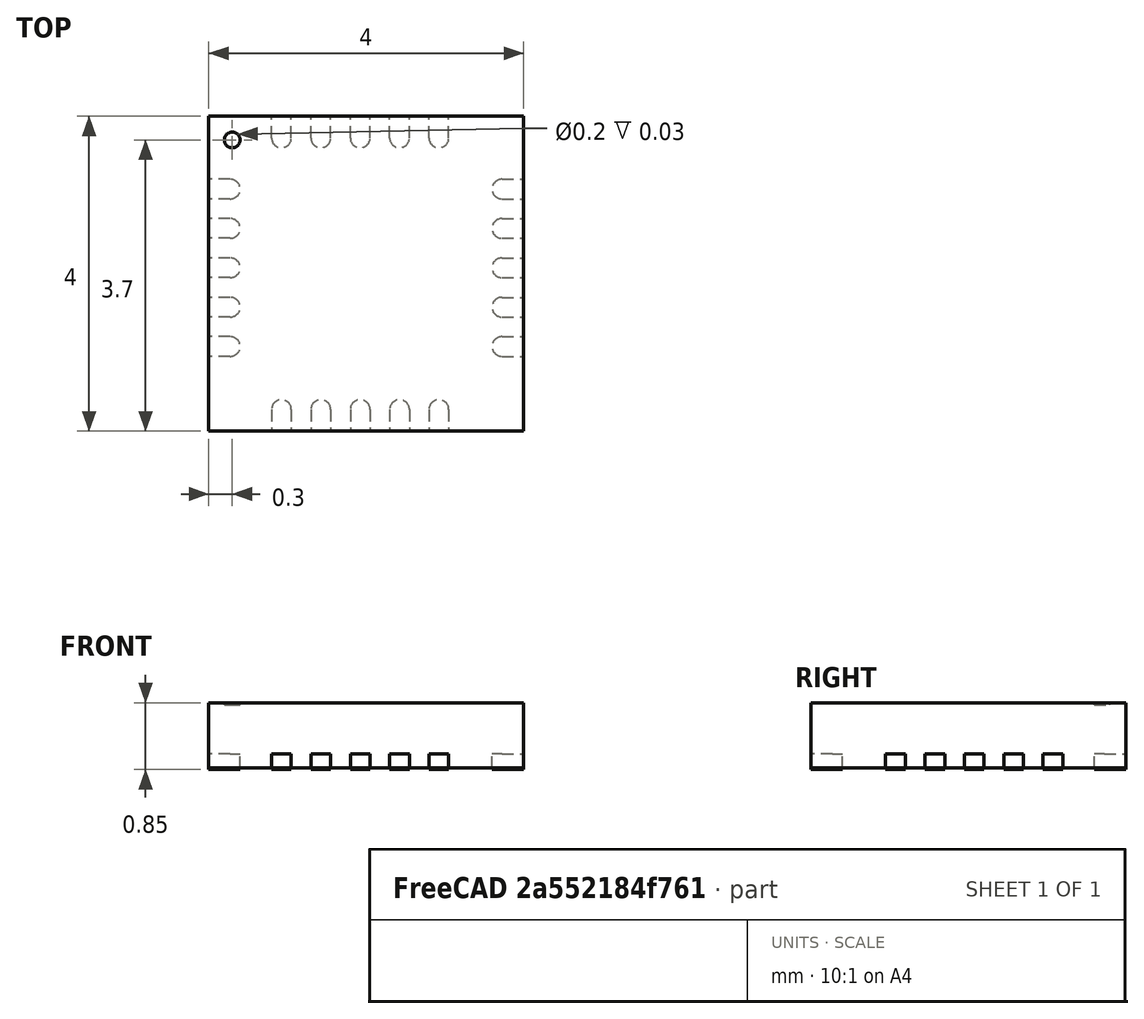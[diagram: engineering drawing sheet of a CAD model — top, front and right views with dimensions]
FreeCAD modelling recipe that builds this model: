
FCSTD DOCUMENT  (FreeCAD 0.14R3702 (Git))
Label: QFN20-5x4
License: CC-BY 3.0
LicenseURL: http://creativecommons.org/licenses/by/3.0/
objects: Part::FeaturePython×4, Part::Box×2, Part::Cylinder×2, Part::MultiFuse×2, Part::Cut×1, App::DocumentObjectGroup×1
note: 11 computed .brp shape members not serialized (recipe doc carries the construction recipe); baked Part::Feature solids carry a one-line shape summary decoded from their .brp

FEATURE [Part::Box] Box  label="Cubo"
  Height = 0.83
  Length = 4
  Width = 4
FEATURE [Part::Cylinder] Cylinder  label="Cilindro"
  Angle = 360
  Height = 0.198
  Placement = pos=(0.3,0.3,0.8) rot=(0,0,1;0rad)
  Radius = 0.1
FEATURE [Part::Cut] Cut  label="body"
  Base = -> Box
  Placement = pos=(0,0,0) rot=(0,0,-1;1.5708rad)
  Tool = -> Cylinder
FEATURE [Part::Cylinder] Cylinder001  label="Cilindro001"
  Angle = 360
  Height = 0.2
  Placement = pos=(0,0.125,0) rot=(0,0,1;0rad)
  Radius = 0.125
FEATURE [Part::Box] Box001  label="Cubo001"
  Height = 0.2
  Length = 0.275
  Width = 0.25
FEATURE [Part::MultiFuse] Fusion  label="pad_001"
  Placement = pos=(0.275,0,-0.02) rot=(0,0,1;3.14159rad)
  Shapes = -> [Cylinder001,Box001]
FEATURE [Part::FeaturePython] Array  # Draft array (typed FeaturePython)
  Angle = 360
  ArrayType = 0
  Axis = (0,0,1)
  Base = -> Fusion
  Center = (0,0,0)
  IntervalX = (1,0,0)
  IntervalY = (0,0.5,0)
  IntervalZ = (0,0,1)
  NumberPolar = 1
  NumberX = 1
  NumberY = 5
  NumberZ = 1
  Placement = pos=(0,-2.8,0) rot=(0,0,1;0rad)
FEATURE [Part::FeaturePython] Clone  label="Clone of Array"  # Draft clone (typed FeaturePython)
  Objects = -> [Array]
  Placement = pos=(4,-1.05,0) rot=(0,0,1;3.14159rad)
  Scale = (1,1,1)
FEATURE [Part::FeaturePython] Clone001  label="Clone of Clone of Array"  # Draft clone (typed FeaturePython)
  Objects = -> [Clone]
  Placement = pos=(1.05,0,0) rot=(0,0,-1;1.5708rad)
  Scale = (1,1,1)
FEATURE [Part::FeaturePython] Clone002  label="Clone of Clone of Clone of Array"  # Draft clone (typed FeaturePython)
  Objects = -> [Clone001]
  Placement = pos=(2.8,-4,0) rot=(0,0,1;1.5708rad)
  Scale = (1,1,1)
FEATURE [Part::MultiFuse] Fusion001  label="pads"
  Shapes = -> [Array,Clone,Clone001,Clone002]
FEATURE [App::DocumentObjectGroup] Grupo  label="QFN20-5x4"
  Group = -> [Cut,Fusion001]
